# Revit family: AP - Generic - 1
name_source: partatom
category: Generic Models
revit_build: Autodesk Revit 2017 (Build: 20160225_1515(x64)
units: mm (PartAtom-declared; Revit-internal decimal feet)

## family parameters
Always vertical = Yes
Can host rebar = No
Cut with Voids When Loaded = No
Part Type = Normal
Room Calculation Point = No
Round Connector Dimension = Use Diameter
Shared = No
Work Plane-Based = No

## types (5) — shared parameters

## per-type parameters (varying)
| type | Altezza | Est_L | Est_XL | Nord_L | Nord_XL | Ovest | Sud |
| Type 1 | 400 mm  [stored 1.31234 ft] | 1900 mm  [stored 6.2336 ft] | 3200 mm  [stored 10.4987 ft] | 2700 mm  [stored 8.85827 ft] | 3700 mm  [stored 12.1391 ft] | 2500 mm  [stored 8.2021 ft] | 1200 mm |
| Type 2 | 750 mm  [stored 2.46063 ft] | 1100 mm | 4400 mm | 1900 mm  [stored 6.2336 ft] | 4100 mm  [stored 13.4514 ft] | 2500 mm  [stored 8.2021 ft] | 1700 mm  [stored 5.57743 ft] |
| Type 3 | 320 mm  [stored 1.04987 ft] | 900 mm  [stored 2.95276 ft] | 3400 mm  [stored 11.1549 ft] | 1900 mm  [stored 6.2336 ft] | 4100 mm  [stored 13.4514 ft] | 2500 mm  [stored 8.2021 ft] | 2400 mm |
| Type 4 | 1270 mm | 1700 mm  [stored 5.57743 ft] | 2400 mm | 1900 mm  [stored 6.2336 ft] | 5100 mm  [stored 16.7323 ft] | 1900 mm  [stored 6.2336 ft] | 2200 mm |
| Type 5 | 1420 mm | 700 mm  [stored 2.29659 ft] | 3200 mm  [stored 10.4987 ft] | 1350 mm  [stored 4.42913 ft] | 4100 mm  [stored 13.4514 ft] | 1800 mm  [stored 5.90551 ft] | 1700 mm  [stored 5.57743 ft] |

note: [stored X ft] marks values corroborated as IEEE doubles in the binary element streams (Revit-internal decimal feet)

## geometry (parser evidence)
native form markers: Sweep x3
no freeform markers — native parametric forms only
